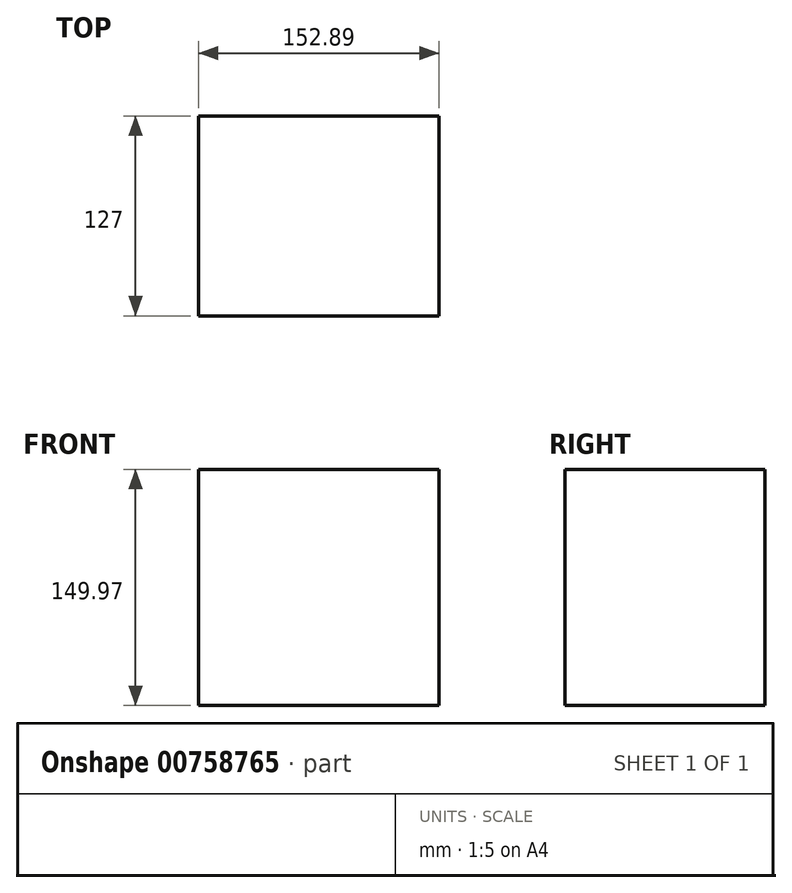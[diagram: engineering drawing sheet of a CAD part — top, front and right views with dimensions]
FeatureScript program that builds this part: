
annotation { "Feature Type Name" : "Feature", "Feature Type Description" : "" }
export const myFeature = defineFeature(function(context is Context, id is Id, definition is map)
    precondition{}
    {
        {
            var Q0;
            Q0=qCreatedBy(makeId("Front.planeOp"),FACE);
            var sketch = newSketch(context, id + "F0", { "sketchPlane" : qUnion([Q0])});
            skLineSegment(sketch, "E0.bottom", {"start": v(-119.64, 92.17) * mm, "end": v(33.25, 92.17) * mm});
            skLineSegment(sketch, "E0.top", {"start": v(-119.64, -57.8) * mm, "end": v(33.25, -57.8) * mm});
            skLineSegment(sketch, "E0.left", {"start": v(-119.64, 92.17) * mm, "end": v(-119.64, -57.8) * mm});
            skLineSegment(sketch, "E0.right", {"start": v(33.25, 92.17) * mm, "end": v(33.25, -57.8) * mm});
            skSolve(sketch);
        }
        {
            var Q0;
            Q0=makeQuery(id+"F0.imprint","IMPRINT",FACE,{"disambiguationData":[TD([[makeQuery(id+"F0.imprint","IMPRINT",EDGE,{"derivedFrom":sQuery(id+"F0.wireOp",EDGE,"E0.bottom")}),-1.0]])]});
            extrude(context, id + "F1", {"entities" : qUnion([Q0]), "depth" : 127 * mm, "offsetDistance" : 25.4 * mm});
        }
    });
